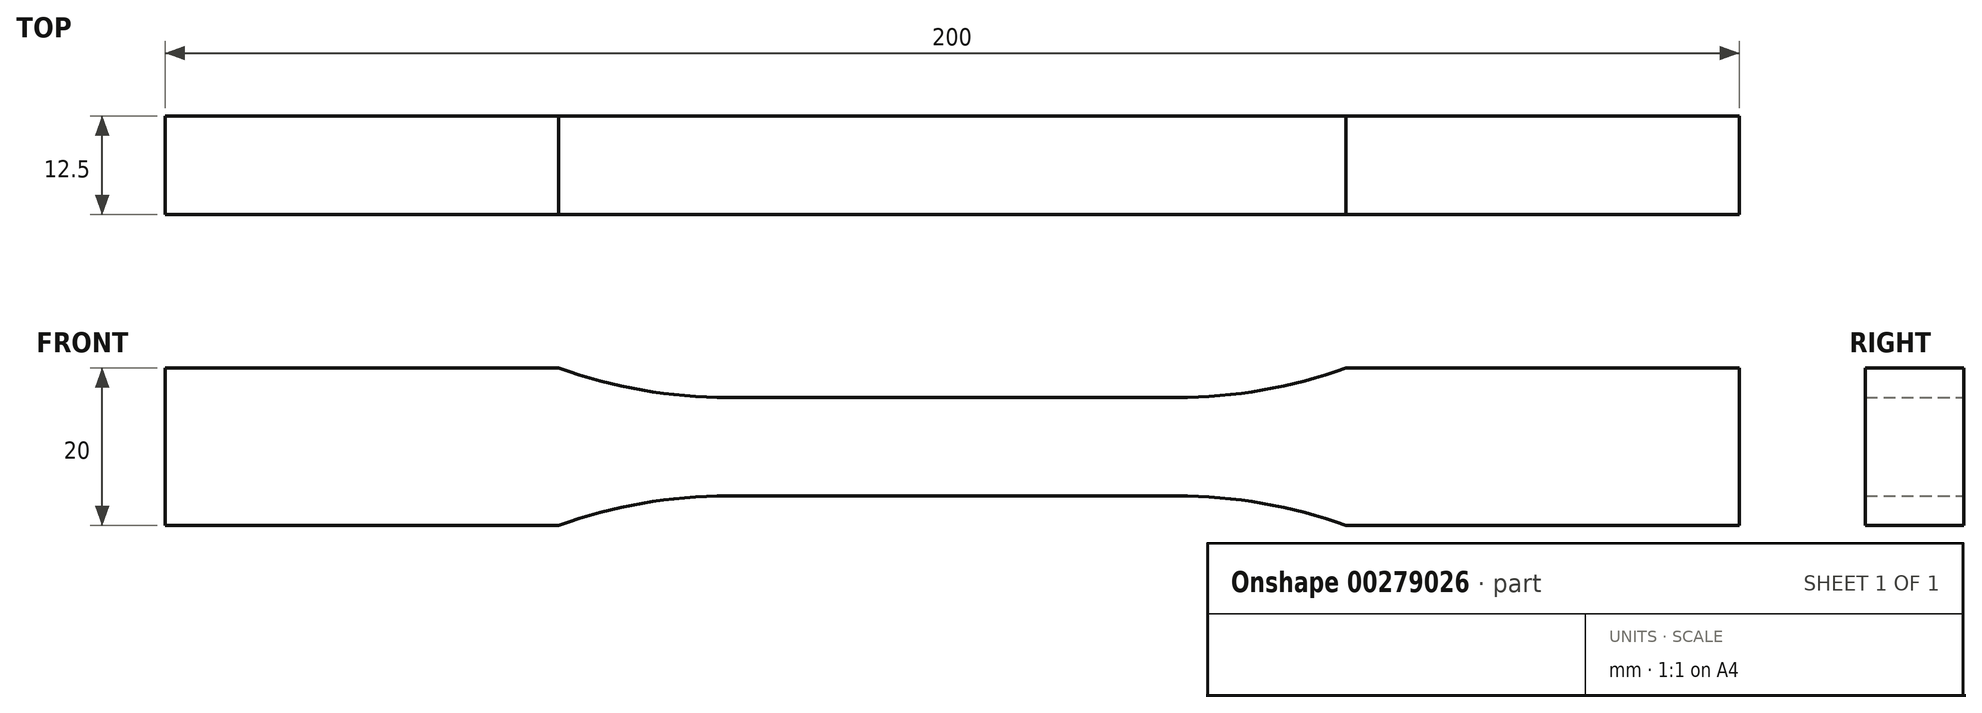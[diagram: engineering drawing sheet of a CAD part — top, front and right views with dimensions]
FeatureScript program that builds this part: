
annotation { "Feature Type Name" : "Feature", "Feature Type Description" : "" }
export const myFeature = defineFeature(function(context is Context, id is Id, definition is map)
    precondition{}
    {
        {
            var Q0;
            Q0=qCreatedBy(makeId("Front.planeOp"),FACE);
            var sketch = newSketch(context, id + "F0", { "sketchPlane" : qUnion([Q0])});
            skLineSegment(sketch, "E0", {"start": v(0, 6.25) * mm, "end": v(28.5, 6.25) * mm});
            skArc(sketch, "E1", {"start": v(28.5, 6.25) * mm, "mid": v(39.41, 7.2) * mm, "end": v(50, 10) * mm});
            skLineSegment(sketch, "E2", {"start": v(50, 10) * mm, "end": v(100, 10) * mm});
            skLineSegment(sketch, "E3", {"start": v(100, 10) * mm, "end": v(100, 0) * mm});
            skLineSegment(sketch, "E4.MirrorCS", {"start": v(0, -6.25) * mm, "end": v(28.5, -6.25) * mm});
            skLineSegment(sketch, "E5.MirrorCS", {"start": v(100, -10) * mm, "end": v(100, 0) * mm});
            skLineSegment(sketch, "E6.MirrorCS", {"start": v(50, -10) * mm, "end": v(100, -10) * mm});
            skArc(sketch, "E7.MirrorCS", {"start": v(28.5, -6.25) * mm, "mid": v(39.41, -7.2) * mm, "end": v(50, -10) * mm});
            skArc(sketch, "E8.MirrorCS", {"start": v(-28.5, -6.25) * mm, "mid": v(-39.41, -7.2) * mm, "end": v(-50, -10) * mm});
            skLineSegment(sketch, "E9.MirrorCS", {"start": v(-50, -10) * mm, "end": v(-100, -10) * mm});
            skArc(sketch, "E10.MirrorCS", {"start": v(-28.5, 6.25) * mm, "mid": v(-39.41, 7.2) * mm, "end": v(-50, 10) * mm});
            skLineSegment(sketch, "E11.MirrorCS", {"start": v(-50, 10) * mm, "end": v(-100, 10) * mm});
            skLineSegment(sketch, "E12.MirrorCS", {"start": v(-100, -10) * mm, "end": v(-100, 0) * mm});
            skLineSegment(sketch, "E13.MirrorCS", {"start": v(0, -6.25) * mm, "end": v(-28.5, -6.25) * mm});
            skLineSegment(sketch, "E14.MirrorCS", {"start": v(-100, 10) * mm, "end": v(-100, 0) * mm});
            skLineSegment(sketch, "E15.MirrorCS", {"start": v(0, 6.25) * mm, "end": v(-28.5, 6.25) * mm});
            skSolve(sketch);
        }
        {
            var Q0;
            Q0=makeQuery(id+"F0.imprint","IMPRINT",FACE,{"disambiguationData":[TD([[makeQuery(id+"F0.imprint","IMPRINT",EDGE,{"derivedFrom":sQuery(id+"F0.wireOp",EDGE,"E0")}),-1.0]])]});
            extrude(context, id + "F1", {"entities" : qUnion([Q0]), "endBound" : BoundingType.SYMMETRIC, "depth" : 12.5 * mm});
        }
    });
